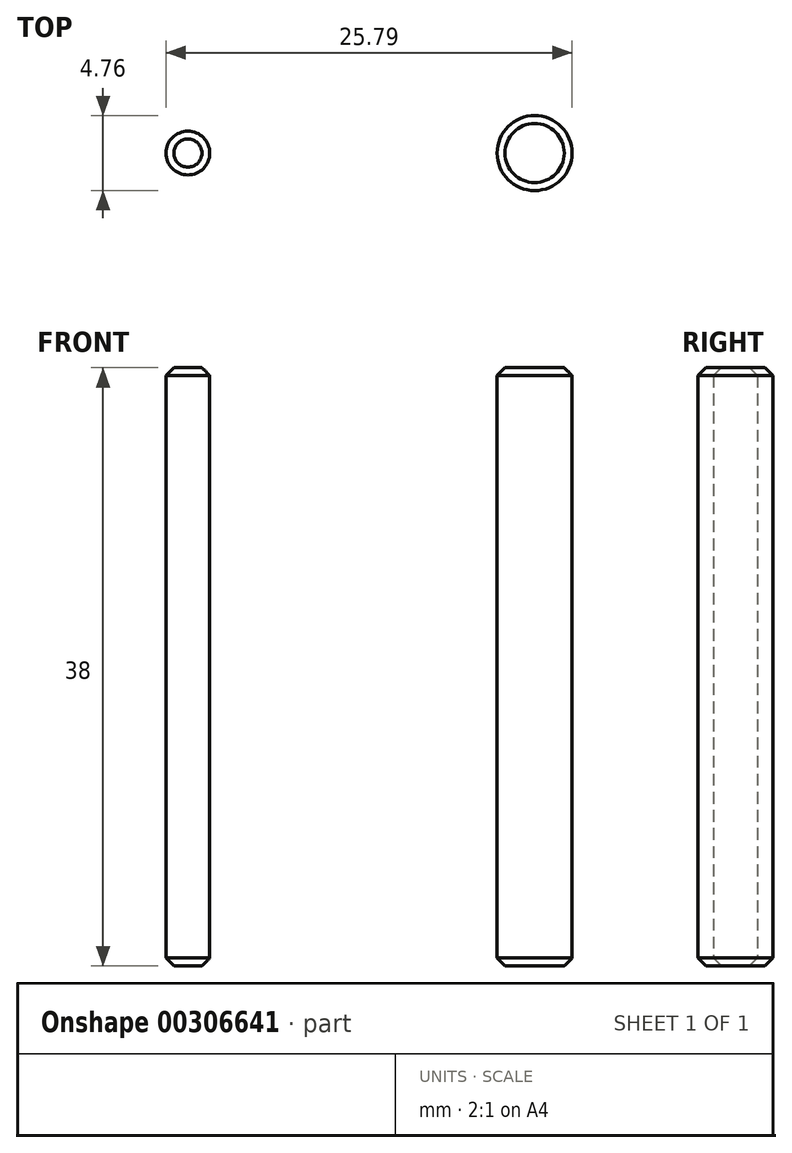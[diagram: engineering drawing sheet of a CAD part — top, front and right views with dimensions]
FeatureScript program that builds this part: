
annotation { "Feature Type Name" : "Feature", "Feature Type Description" : "" }
export const myFeature = defineFeature(function(context is Context, id is Id, definition is map)
    precondition{}
    {
        {
            var Q0;
            Q0=qCreatedBy(makeId("Top.planeOp"),FACE);
            var sketch = newSketch(context, id + "F0", { "sketchPlane" : qUnion([Q0])});
            skCircle(sketch, "E0", {"center": v(-12.5, 0) * mm, "radius": 1.39 * mm});
            skCircle(sketch, "E1", {"center": v(9.52, 0) * mm, "radius": 2.38 * mm});
            skSolve(sketch);
        }
        {
            var Q0;
            Q0=makeQuery(id+"F0.imprint","IMPRINT",FACE,{"disambiguationData":[TD([[makeQuery(id+"F0.imprint","IMPRINT",EDGE,{"derivedFrom":sQuery(id+"F0.wireOp",EDGE,"E0")}),1.0]])]});
            var Q1;
            Q1=makeQuery(id+"F0.imprint","IMPRINT",FACE,{"disambiguationData":[TD([[makeQuery(id+"F0.imprint","IMPRINT",EDGE,{"derivedFrom":sQuery(id+"F0.wireOp",EDGE,"E1")}),1.0]])]});
            extrude(context, id + "F1", {"entities" : qUnion([Q0, Q1]), "depth" : 38 * mm});
        }
        {
            var Q0;
            Q0=makeQuery(id+"F1.opExtrude","CAP_EDGE",EDGE,{"disambiguationData":[OSD([sQuery(id+"F0.wireOp",EDGE,"E0")])],"isStart":false});
            var Q1;
            Q1=makeQuery(id+"F1.opExtrude","CAP_EDGE",EDGE,{"disambiguationData":[OSD([sQuery(id+"F0.wireOp",EDGE,"E1")])],"isStart":false});
            var Q2;
            Q2=makeQuery(id+"F1.opExtrude","CAP_EDGE",EDGE,{"disambiguationData":[OSD([sQuery(id+"F0.wireOp",EDGE,"E1")])],"isStart":true});
            var Q3;
            Q3=makeQuery(id+"F1.opExtrude","CAP_EDGE",EDGE,{"disambiguationData":[OSD([sQuery(id+"F0.wireOp",EDGE,"E0")])],"isStart":true});
            chamfer(context, id + "F2", {"entities" : qUnion([Q0, Q1, Q2, Q3]), "width" : 0.5 * mm, "tangentPropagation" : true});
        }
    });
